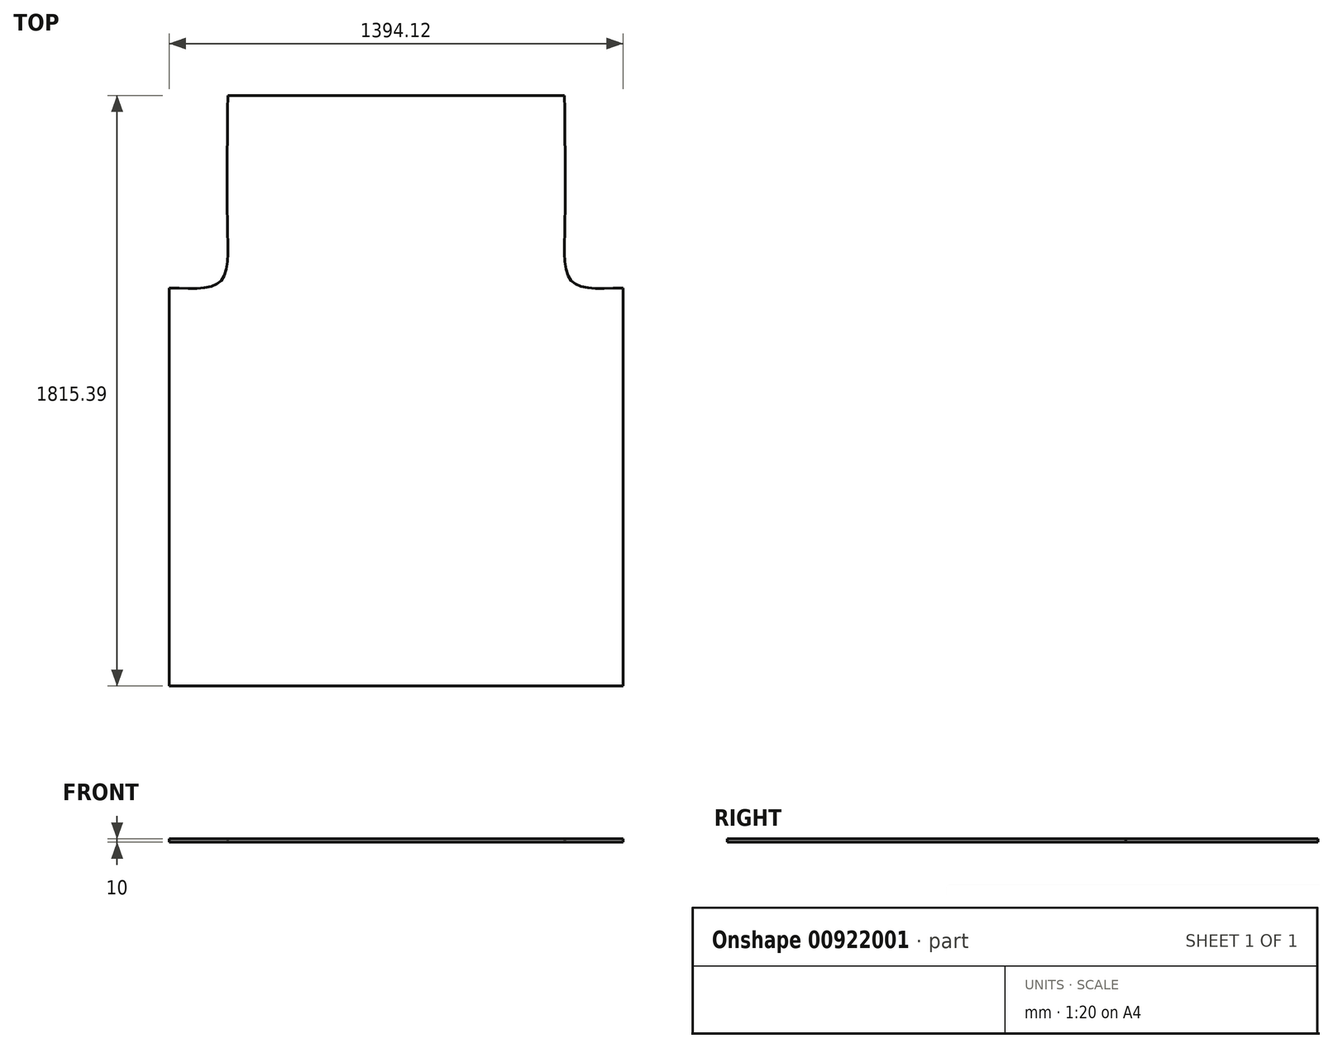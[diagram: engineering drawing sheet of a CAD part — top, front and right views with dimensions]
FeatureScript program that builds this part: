
annotation { "Feature Type Name" : "Feature", "Feature Type Description" : "" }
export const myFeature = defineFeature(function(context is Context, id is Id, definition is map)
    precondition{}
    {
        {
            var Q0;
            Q0=qCreatedBy(makeId("Top.planeOp"),FACE);
            var sketch = newSketch(context, id + "F0", { "sketchPlane" : qUnion([Q0])});
            skLineSegment(sketch, "E0.bottom", {"start": v(697.06, 85.16) * mm, "end": v(0, 85.16) * mm});
            skLineSegment(sketch, "E0.top", {"start": v(697.06, 1900.55) * mm, "end": v(0, 1900.55) * mm});
            skLineSegment(sketch, "E0.left", {"start": v(697.06, 85.16) * mm, "end": v(697.06, 1900.55) * mm});
            skLineSegment(sketch, "E0.right", {"start": v(0, 85.16) * mm, "end": v(0, 1900.55) * mm});
            skSolve(sketch);
        }
        {
            var Q0;
            Q0=makeQuery(id+"F0.imprint","IMPRINT",FACE,{"disambiguationData":[TD([[makeQuery(id+"F0.imprint","IMPRINT",EDGE,{"derivedFrom":sQuery(id+"F0.wireOp",EDGE,"E0.bottom")}),-1.0]])]});
            extrude(context, id + "F1", {"entities" : qUnion([Q0]), "oppositeDirection" : true, "depth" : 10 * mm, "offsetDistance" : 25 * mm});
        }
        {
            var Q0;
            Q0=makeQuery(id+"F1.opExtrude","CAP_FACE",FACE,{"disambiguationData":[OSD([sQuery(id+"F0.wireOp",EDGE,"E0.bottom"),sQuery(id+"F0.wireOp",EDGE,"E0.top"),sQuery(id+"F0.wireOp",EDGE,"E0.left"),sQuery(id+"F0.wireOp",EDGE,"E0.right")])],"isStart":true});
            var sketch = newSketch(context, id + "F2", { "sketchPlane" : qUnion([Q0])});
            skLineSegment(sketch, "E1", {"start": v(731.56, 1309.24) * mm, "end": v(731.56, 2029) * mm});
            skLineSegment(sketch, "E2", {"start": v(731.56, 2029) * mm, "end": v(518.8, 2038.9) * mm});
            skFitSpline(sketch, "E3", {"points": [v(518.8, 2038.9) * mm, v(518.8, 1516.91) * mm, v(544.94, 1325.05) * mm, v(731.56, 1309.24) * mm], "startDerivative": vector(-29.08, -916.4) * mm, "endDerivative": vector(876.97, -15.95) * mm});
            skSolve(sketch);
        }
        {
            var Q0;
            Q0 = qSketchRegion(id + "F2", true);
            extrude(context, id + "F3", {"entities" : qUnion([Q0]), "operationType" : NewBodyOperationType.REMOVE, "oppositeDirection" : true, "depth" : 660 * mm, "offsetDistance" : 25 * mm});
        }
        {
            var Q0;
            Q0=makeQuery(id+"F1.opExtrude","SWEPT_BODY",BODY,{"disambiguationData":[OSD([sQuery(id+"F0.wireOp",EDGE,"E0.bottom"),sQuery(id+"F0.wireOp",EDGE,"E0.top"),sQuery(id+"F0.wireOp",EDGE,"E0.left"),sQuery(id+"F0.wireOp",EDGE,"E0.right")])]});
            var Q1;
            Q1=qCreatedBy(makeId("Right.planeOp"),FACE);
            mirror(context, id + "F4", {"operationType" : NewBodyOperationType.ADD, "entities" : qUnion([Q0]), "mirrorPlane" : qUnion([Q1])});
        }
    });
